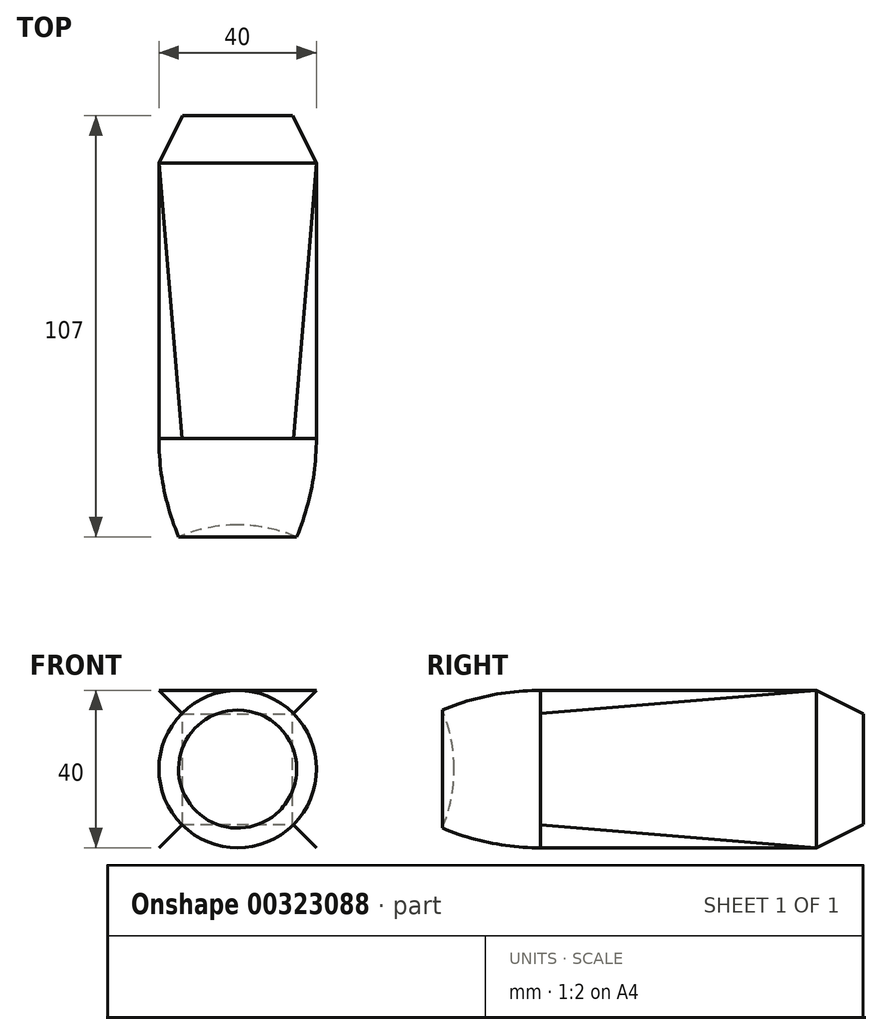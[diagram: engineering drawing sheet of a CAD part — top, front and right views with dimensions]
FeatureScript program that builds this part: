
annotation { "Feature Type Name" : "Feature", "Feature Type Description" : "" }
export const myFeature = defineFeature(function(context is Context, id is Id, definition is map)
    precondition{}
    {
        {
            var Q0;
            Q0=qCreatedBy(makeId("Front.planeOp"),FACE);
            var sketch = newSketch(context, id + "F0", { "sketchPlane" : qUnion([Q0])});
            skLineSegment(sketch, "E0.bottom", {"start": v(0, 0) * mm, "end": v(40, 0) * mm});
            skLineSegment(sketch, "E0.top", {"start": v(0, 40) * mm, "end": v(40, 40) * mm});
            skLineSegment(sketch, "E0.left", {"start": v(0, 0) * mm, "end": v(0, 40) * mm});
            skLineSegment(sketch, "E0.right", {"start": v(40, 0) * mm, "end": v(40, 40) * mm});
            skSolve(sketch);
        }
        {
            var Q0;
            Q0=qCreatedBy(makeId("Front.planeOp"),FACE);
            cPlane(context, id + "F1", {"entities" : qUnion([Q0]), "cplaneType" : CPlaneType.OFFSET, "offset" : 70 * mm, "width" : 150 * mm, "height" : 150 * mm});
        }
        {
            var Q0;
            Q0=qCreatedBy(id+"F1.planeOp",FACE);
            var sketch = newSketch(context, id + "F2", { "sketchPlane" : qUnion([Q0])});
            skCircle(sketch, "E1", {"center": v(20, 20) * mm, "radius": 20 * mm});
            skSolve(sketch);
        }
        {
            var Q0;
            Q0=makeQuery(id+"F0.imprint","IMPRINT",FACE,{"disambiguationData":[TD([[makeQuery(id+"F0.imprint","IMPRINT",EDGE,{"derivedFrom":sQuery(id+"F0.wireOp",EDGE,"E0.bottom")}),1.0]])]});
            var Q1;
            Q1=makeQuery(id+"F2.imprint","IMPRINT",FACE,{"disambiguationData":[TD([[makeQuery(id+"F2.imprint","IMPRINT",EDGE,{"derivedFrom":sQuery(id+"F2.wireOp",EDGE,"E1")}),1.0]])]});
            loft(context, id + "F3", {"sheetProfilesArray" : [{ "sheetProfileEntities" : qUnion([Q0]) }, { "sheetProfileEntities" : qUnion([Q1]) }]});
        }
        {
            var Q0;
            Q0=qCreatedBy(makeId("Front.planeOp"),FACE);
            cPlane(context, id + "F4", {"entities" : qUnion([Q0]), "cplaneType" : CPlaneType.OFFSET, "offset" : 12 * mm, "oppositeDirection" : true, "width" : 150 * mm, "height" : 150 * mm});
        }
        {
            var Q0;
            Q0=qCreatedBy(id+"F4.planeOp",FACE);
            var sketch = newSketch(context, id + "F5", { "sketchPlane" : qUnion([Q0])});
            skLineSegment(sketch, "E2.bottom", {"start": v(6, 6) * mm, "end": v(34, 6) * mm});
            skLineSegment(sketch, "E2.top", {"start": v(6, 34) * mm, "end": v(34, 34) * mm});
            skLineSegment(sketch, "E2.left", {"start": v(6, 6) * mm, "end": v(6, 34) * mm});
            skLineSegment(sketch, "E2.right", {"start": v(34, 6) * mm, "end": v(34, 34) * mm});
            skSolve(sketch);
        }
        {
            var Q1;
            Q1=makeQuery(id+"F5.imprint","IMPRINT",FACE,{"disambiguationData":[TD([[makeQuery(id+"F5.imprint","IMPRINT",EDGE,{"derivedFrom":sQuery(id+"F5.wireOp",EDGE,"E2.bottom")}),1.0]])]});
            var Q2;
            Q2=makeQuery(id+"F3.opLoft","CAP_FACE",FACE,{"disambiguationData":[OSD([makeQuery(id+"F0.imprint","IMPRINT",FACE,{"disambiguationData":[TD([[makeQuery(id+"F0.imprint","IMPRINT",EDGE,{"derivedFrom":sQuery(id+"F0.wireOp",EDGE,"E0.bottom")}),1.0]])]})])],"isStart":true});
            loft(context, id + "F6", {"operationType" : NewBodyOperationType.ADD, "sheetProfilesArray" : [{ "sheetProfileEntities" : qUnion([Q1]) }, { "sheetProfileEntities" : qUnion([Q2]) }]});
        }
        {
            var Q0;
            Q0=qCreatedBy(makeId("Top.planeOp"),FACE);
            cPlane(context, id + "F7", {"entities" : qUnion([Q0]), "cplaneType" : CPlaneType.OFFSET, "offset" : 20 * mm, "width" : 150 * mm, "height" : 150 * mm});
        }
        {
            var Q0;
            Q0=qCreatedBy(id+"F7.planeOp",FACE);
            var sketch = newSketch(context, id + "F8", { "sketchPlane" : qUnion([Q0])});
            skLineSegment(sketch, "E3", {"start": v(20, -70) * mm, "end": v(20, -92) * mm});
            skLineSegment(sketch, "E4", {"start": v(20, -95) * mm, "end": v(35, -95) * mm, "construction": true});
            skArc(sketch, "E5", {"start": v(35, -95) * mm, "mid": v(27.65, -92.76) * mm, "end": v(20, -92) * mm});
            skLineSegment(sketch, "E6", {"start": v(20, -70) * mm, "end": v(40, -70) * mm});
            skLineSegment(sketch, "E7", {"start": v(40, -70) * mm, "end": v(40, -127.77) * mm, "construction": true});
            skArc(sketch, "E8", {"start": v(35, -95) * mm, "mid": v(38.74, -82.75) * mm, "end": v(40, -70) * mm});
            skLineSegment(sketch, "E9", {"start": v(20, -92) * mm, "end": v(20, -95) * mm, "construction": true});
            skSolve(sketch);
        }
        {
            var Q0;
            Q0=makeQuery(id+"F8.imprint","IMPRINT",FACE,{"disambiguationData":[TD([[makeQuery(id+"F8.imprint","IMPRINT",EDGE,{"derivedFrom":sQuery(id+"F8.wireOp",EDGE,"E3")}),1.0]])]});
            var Q1;
            Q1=sQuery(id+"F8.wireOp",EDGE,"E9");
            revolve(context, id + "F9", {"operationType" : NewBodyOperationType.ADD, "entities" : qUnion([Q0]), "axis" : qUnion([Q1]), "revolveType" : RevolveType.FULL});
        }
    });
